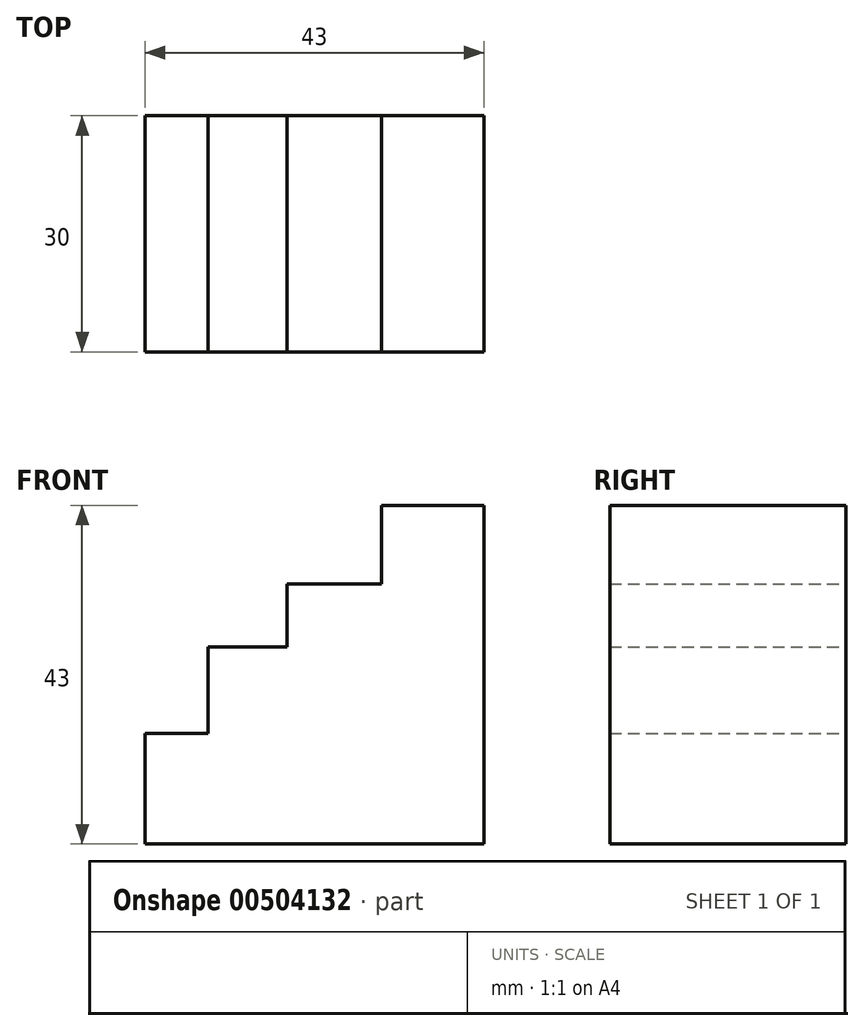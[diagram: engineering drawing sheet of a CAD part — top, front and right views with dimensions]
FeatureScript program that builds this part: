
annotation { "Feature Type Name" : "Feature", "Feature Type Description" : "" }
export const myFeature = defineFeature(function(context is Context, id is Id, definition is map)
    precondition{}
    {
        {
            var Q0;
            Q0=qCreatedBy(makeId("Front.planeOp"),FACE);
            var sketch = newSketch(context, id + "F0", { "sketchPlane" : qUnion([Q0])});
            skLineSegment(sketch, "E0.bottom", {"start": v(0, 0) * mm, "end": v(13, 0) * mm});
            skLineSegment(sketch, "E0.top", {"start": v(0, 43) * mm, "end": v(13, 43) * mm});
            skLineSegment(sketch, "E0.left", {"start": v(0, 0) * mm, "end": v(0, 43) * mm});
            skLineSegment(sketch, "E0.right", {"start": v(13, 0) * mm, "end": v(13, 43) * mm});
            skLineSegment(sketch, "E1.bottom", {"start": v(13, 33) * mm, "end": v(25, 33) * mm});
            skLineSegment(sketch, "E1.top", {"start": v(13, 0) * mm, "end": v(25, 0) * mm});
            skLineSegment(sketch, "E1.left", {"start": v(13, 33) * mm, "end": v(13, 0) * mm});
            skLineSegment(sketch, "E1.right", {"start": v(25, 33) * mm, "end": v(25, 0) * mm});
            skLineSegment(sketch, "E2.bottom", {"start": v(25, 25) * mm, "end": v(35, 25) * mm});
            skLineSegment(sketch, "E2.top", {"start": v(25, 0) * mm, "end": v(35, 0) * mm});
            skLineSegment(sketch, "E2.left", {"start": v(25, 25) * mm, "end": v(25, 0) * mm});
            skLineSegment(sketch, "E2.right", {"start": v(35, 25) * mm, "end": v(35, 0) * mm});
            skLineSegment(sketch, "E3.bottom", {"start": v(35, 14) * mm, "end": v(43, 14) * mm});
            skLineSegment(sketch, "E3.top", {"start": v(35, 0) * mm, "end": v(43, 0) * mm});
            skLineSegment(sketch, "E3.left", {"start": v(35, 14) * mm, "end": v(35, 0) * mm});
            skLineSegment(sketch, "E3.right", {"start": v(43, 14) * mm, "end": v(43, 0) * mm});
            skLineSegment(sketch, "E4.MirrorCS", {"start": v(0, 43) * mm, "end": v(-13, 43) * mm});
            skLineSegment(sketch, "E5.MirrorCS", {"start": v(-13, 0) * mm, "end": v(-13, 43) * mm});
            skLineSegment(sketch, "E6.MirrorCS", {"start": v(-13, 33) * mm, "end": v(-25, 33) * mm});
            skLineSegment(sketch, "E7.MirrorCS", {"start": v(-25, 25) * mm, "end": v(-35, 25) * mm});
            skLineSegment(sketch, "E8.MirrorCS", {"start": v(-35, 14) * mm, "end": v(-43, 14) * mm});
            skLineSegment(sketch, "E9.MirrorCS", {"start": v(-43, 14) * mm, "end": v(-43, 0) * mm});
            skLineSegment(sketch, "E10.MirrorCS", {"start": v(-35, 25) * mm, "end": v(-35, 0) * mm});
            skLineSegment(sketch, "E11.MirrorCS", {"start": v(-25, 25) * mm, "end": v(-25, 0) * mm});
            skLineSegment(sketch, "E12.MirrorCS", {"start": v(-13, 0) * mm, "end": v(-25, 0) * mm});
            skLineSegment(sketch, "E13.MirrorCS", {"start": v(0, 0) * mm, "end": v(-13, 0) * mm});
            skLineSegment(sketch, "E14.MirrorCS", {"start": v(-35, 0) * mm, "end": v(-43, 0) * mm});
            skLineSegment(sketch, "E15.MirrorCS", {"start": v(-25, 33) * mm, "end": v(-25, 0) * mm});
            skLineSegment(sketch, "E16.MirrorCS", {"start": v(-25, 0) * mm, "end": v(-35, 0) * mm});
            skSolve(sketch);
        }
        {
            var Q0;
            {var subQ0=sQuery(id+"F0.wireOp",EDGE,"E8.MirrorCS");Q0=makeQuery(id+"F0.imprint","IMPRINT",FACE,{"disambiguationData":[TD([[makeQuery(id+"F0.imprint","IMPRINT",EDGE,{"derivedFrom":subQ0}),1.0]])]});}
            var Q1;
            Q1=makeQuery(id+"F0.imprint","IMPRINT",FACE,{"disambiguationData":[TD([[makeQuery(id+"F0.imprint","IMPRINT",EDGE,{"derivedFrom":sQuery(id+"F0.wireOp",EDGE,"E0.left")}),1.0]])]});
            var Q2;
            {var subQ1=sQuery(id+"F0.wireOp",EDGE,"E6.MirrorCS");Q2=makeQuery(id+"F0.imprint","IMPRINT",FACE,{"disambiguationData":[TD([[makeQuery(id+"F0.imprint","IMPRINT",EDGE,{"derivedFrom":subQ1}),1.0]])]});}
            var Q3;
            {var subQ1=sQuery(id+"F0.wireOp",EDGE,"E7.MirrorCS");Q3=makeQuery(id+"F0.imprint","IMPRINT",FACE,{"disambiguationData":[TD([[makeQuery(id+"F0.imprint","IMPRINT",EDGE,{"derivedFrom":subQ1}),1.0]])]});}
            extrude(context, id + "F1", {"entities" : qUnion([Q0, Q1, Q2, Q3]), "depth" : 30 * mm});
        }
    });
